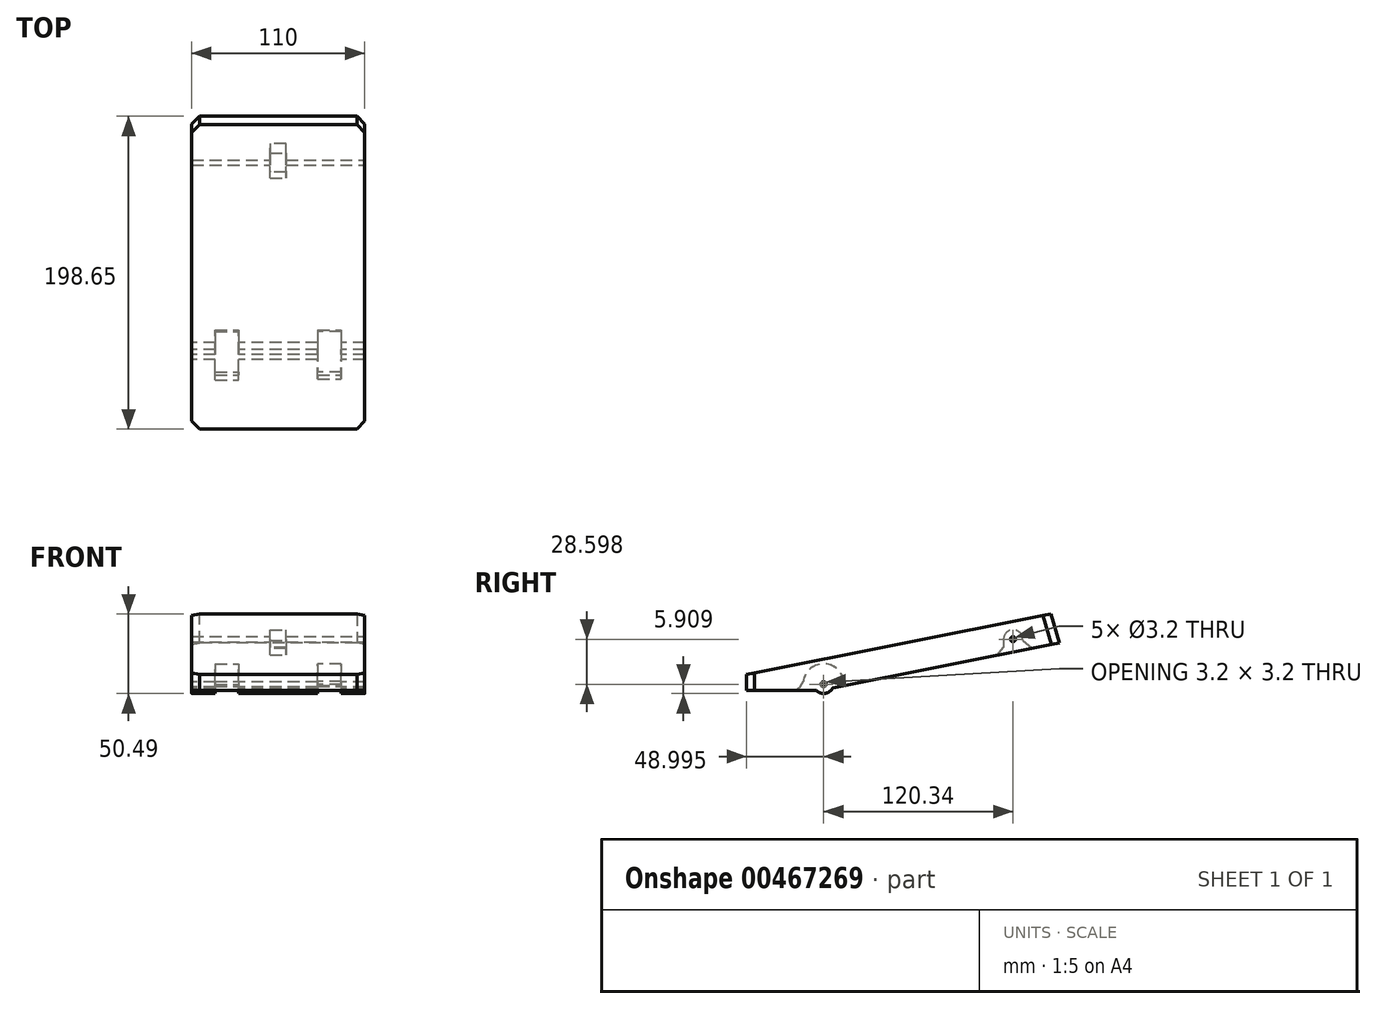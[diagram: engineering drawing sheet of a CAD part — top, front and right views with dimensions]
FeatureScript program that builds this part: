
annotation { "Feature Type Name" : "Feature", "Feature Type Description" : "" }
export const myFeature = defineFeature(function(context is Context, id is Id, definition is map)
    precondition{}
    {
        {
            var Q0;
            Q0=qCreatedBy(makeId("Right.planeOp"),FACE);
            cPlane(context, id + "F0", {"entities" : qUnion([Q0]), "cplaneType" : CPlaneType.OFFSET, "offset" : 55 * mm, "width" : 150 * mm, "height" : 150 * mm});
        }
        {
            var Q0;
            Q0=qCreatedBy(makeId("Right.planeOp"),FACE);
            var sketch = newSketch(context, id + "F1", { "sketchPlane" : qUnion([Q0])});
            skCircle(sketch, "E0.0", {"center": v(-48.56, 3.8) * mm, "radius": 1.6 * mm});
            skArc(sketch, "E1", {"start": v(-53.35, 0) * mm, "mid": v(-47.61, -2.03) * mm, "end": v(-42.71, 1.57) * mm});
            skLineSegment(sketch, "E2", {"start": v(-42.71, 1.57) * mm, "end": v(101.09, 30.13) * mm});
            skLineSegment(sketch, "E3", {"start": v(-97.56, 0) * mm, "end": v(-97.56, 10) * mm});
            skLineSegment(sketch, "E4", {"start": v(-97.56, 10) * mm, "end": v(95.78, 48.39) * mm});
            skLineSegment(sketch, "E5", {"start": v(-53.35, 0) * mm, "end": v(-97.56, 0) * mm});
            skLineSegment(sketch, "E6", {"start": v(95.78, 48.39) * mm, "end": v(101.09, 30.13) * mm});
            skSolve(sketch);
        }
        {
            var Q0;
            Q0=qSketchRegion(id+"F1",true);
            extrude(context, id + "F2", {"entities" : qUnion([Q0]), "depth" : 110 * mm});
        }
        {
            var Q0;
            Q0=qCreatedBy(makeId("Top.planeOp"),FACE);
            var sketch = newSketch(context, id + "F3", { "sketchPlane" : qUnion([Q0])});
            skLineSegment(sketch, "E7.bottom", {"start": v(15, -55.85) * mm, "end": v(30, -55.85) * mm});
            skLineSegment(sketch, "E7.top", {"start": v(15, -40.85) * mm, "end": v(30, -40.85) * mm});
            skLineSegment(sketch, "E7.left", {"start": v(15, -55.85) * mm, "end": v(15, -40.85) * mm});
            skLineSegment(sketch, "E7.right", {"start": v(30, -55.85) * mm, "end": v(30, -40.85) * mm});
            skLineSegment(sketch, "E8.bottom", {"start": v(80, -55.21) * mm, "end": v(95, -55.21) * mm});
            skLineSegment(sketch, "E8.top", {"start": v(80, -40.21) * mm, "end": v(95, -40.21) * mm});
            skLineSegment(sketch, "E8.left", {"start": v(80, -55.21) * mm, "end": v(80, -40.21) * mm});
            skLineSegment(sketch, "E8.right", {"start": v(95, -55.21) * mm, "end": v(95, -40.21) * mm});
            skSolve(sketch);
        }
        {
            var Q0;
            Q0=qSketchRegion(id+"F3",true);
            extrude(context, id + "F4", {"entities" : qUnion([Q0]), "operationType" : NewBodyOperationType.REMOVE, "endBound" : BoundingType.SYMMETRIC, "depth" : 21 * mm});
        }
        {
            var Q0;
            Q0=makeQuery(id+"F4.boolean.opBoolean","COPY",FACE,{"derivedFrom":makeQuery(id+"F4.opExtrude","SWEPT_FACE",FACE,{"disambiguationData":[OSD([sQuery(id+"F3.wireOp",EDGE,"E8.left")])]})});
            var sketch = newSketch(context, id + "F5", { "sketchPlane" : qUnion([Q0])});
            skCircle(sketch, "E9.0", {"center": v(-48.56, 3.8) * mm, "radius": 1.6 * mm});
            skArc(sketch, "E10", {"start": v(-35.56, 3.8) * mm, "mid": v(-48.56, 16.8) * mm, "end": v(-61.56, 3.8) * mm});
            skPoint(sketch, "E11.orphan", {"position": v(-97.56, 0) * mm});
            skPoint(sketch, "E12.orphan", {"position": v(-42.71, 1.57) * mm});
            skPoint(sketch, "E13.0.start.orphan", {"position": v(-53.35, 0) * mm});
            skLineSegment(sketch, "E14", {"start": v(-61.56, 3.8) * mm, "end": v(-67.66, -1.5) * mm});
            skLineSegment(sketch, "E15", {"start": v(-67.66, -1.5) * mm, "end": v(-44.57, -13.85) * mm});
            skLineSegment(sketch, "E16", {"start": v(-44.57, -13.85) * mm, "end": v(-28.97, -1.5) * mm});
            skLineSegment(sketch, "E17", {"start": v(-28.97, -1.5) * mm, "end": v(-35.56, 3.8) * mm});
            skPoint(sketch, "E18.end.orphan", {"position": v(0, 3.8) * mm});
            skPoint(sketch, "E19.end.orphan", {"position": v(-61.56, 0) * mm});
            skSolve(sketch);
        }
        {
            var Q0;
            Q0=qSketchRegion(id+"F5",true);
            var Q1;
            Q1=makeQuery(id+"F4.boolean.opBoolean","INTERSECT",VERTEX,{"derivedFrom":[makeQuery(id+"F2.opExtrude","SWEPT_FACE",FACE,{"disambiguationData":[OSD([sQuery(id+"F1.wireOp",EDGE,"E5")])]}),makeQuery(id+"F4.opExtrude","SWEPT_FACE",FACE,{"disambiguationData":[OSD([sQuery(id+"F3.wireOp",EDGE,"E8.bottom")])]}),makeQuery(id+"F4.opExtrude","SWEPT_FACE",FACE,{"disambiguationData":[OSD([sQuery(id+"F3.wireOp",EDGE,"E8.right")])]})]});
            extrude(context, id + "F6", {"entities" : qUnion([Q0]), "operationType" : NewBodyOperationType.REMOVE, "endBound" : BoundingType.UP_TO_VERTEX, "endBoundEntityVertex" : qUnion([Q1]), "depth" : 25 * mm});
        }
        {
            var Q0;
            Q0=makeQuery(id+"F6.boolean.opBoolean","COPY",EDGE,{"derivedFrom":makeQuery(id+"F6.opExtrude","SWEPT_EDGE",EDGE,{"disambiguationData":[OSD([sQuery(id+"F5.wireOp",EDGE,"E10"),sQuery(id+"F5.wireOp",EDGE,"E14")])]})});
            chamfer(context, id + "F7", {"entities" : qUnion([Q0]), "width" : 5 * mm, "tangentPropagation" : true});
        }
        {
            var Q0;
            Q0=qCreatedBy(id+"F0.planeOp",FACE);
            var sketch = newSketch(context, id + "F8", { "sketchPlane" : qUnion([Q0])});
            skArc(sketch, "E20", {"start": v(77.78, 32.4) * mm, "mid": v(71.78, 38.4) * mm, "end": v(65.78, 32.4) * mm});
            skLineSegment(sketch, "E21", {"start": v(65.78, 32.4) * mm, "end": v(65.78, 22.07) * mm});
            skLineSegment(sketch, "E22", {"start": v(77.78, 32.4) * mm, "end": v(77.78, 22.07) * mm});
            skLineSegment(sketch, "E23", {"start": v(65.78, 22.07) * mm, "end": v(77.78, 22.07) * mm});
            skSolve(sketch);
        }
        {
            var Q0;
            Q0=qSketchRegion(id+"F8",true);
            extrude(context, id + "F9", {"entities" : qUnion([Q0]), "operationType" : NewBodyOperationType.REMOVE, "endBound" : BoundingType.SYMMETRIC, "oppositeDirection" : true, "depth" : 10 * mm});
        }
        {
            var Q0;
            Q0=makeQuery(id+"F2.opExtrude","CAP_FACE",FACE,{"disambiguationData":[OSD([sQuery(id+"F1.wireOp",EDGE,"E0.0"),sQuery(id+"F1.wireOp",EDGE,"E1"),sQuery(id+"F1.wireOp",EDGE,"E2"),sQuery(id+"F1.wireOp",EDGE,"E3"),sQuery(id+"F1.wireOp",EDGE,"E4"),sQuery(id+"F1.wireOp",EDGE,"E5"),sQuery(id+"F1.wireOp",EDGE,"E6")])],"isStart":false});
            var sketch = newSketch(context, id + "F10", { "sketchPlane" : qUnion([Q0])});
            skCircle(sketch, "E24", {"center": v(71.78, 32.4) * mm, "radius": 1.6 * mm});
            skSolve(sketch);
        }
        {
            var Q0;
            Q0=qSketchRegion(id+"F10",true);
            extrude(context, id + "F11", {"entities" : qUnion([Q0]), "operationType" : NewBodyOperationType.REMOVE, "endBound" : BoundingType.THROUGH_ALL, "oppositeDirection" : true, "depth" : 25 * mm});
        }
        {
            var Q0;
            Q0=makeQuery(id+"F9.boolean.opBoolean","INTERSECT",EDGE,{"derivedFrom":[makeQuery(id+"F2.opExtrude","SWEPT_FACE",FACE,{"disambiguationData":[OSD([sQuery(id+"F1.wireOp",EDGE,"E2")])]}),makeQuery(id+"F9.opExtrude","SWEPT_FACE",FACE,{"disambiguationData":[OSD([sQuery(id+"F8.wireOp",EDGE,"E22")])]})]});
            chamfer(context, id + "F12", {"entities" : qUnion([Q0]), "width" : 5 * mm, "tangentPropagation" : true});
        }
        {
            var Q0;
            Q0=makeQuery(id+"F9.boolean.opBoolean","INTERSECT",EDGE,{"derivedFrom":[makeQuery(id+"F2.opExtrude","SWEPT_FACE",FACE,{"disambiguationData":[OSD([sQuery(id+"F1.wireOp",EDGE,"E2")])]}),makeQuery(id+"F9.opExtrude","SWEPT_FACE",FACE,{"disambiguationData":[OSD([sQuery(id+"F8.wireOp",EDGE,"E21")])]})]});
            chamfer(context, id + "F13", {"entities" : qUnion([Q0]), "width" : 5 * mm, "tangentPropagation" : true});
        }
        {
            var Q0;
            Q0=makeQuery(id+"F2.opExtrude","CAP_EDGE",EDGE,{"disambiguationData":[OSD([sQuery(id+"F1.wireOp",EDGE,"E6")])],"isStart":true});
            var Q1;
            Q1=makeQuery(id+"F2.opExtrude","CAP_EDGE",EDGE,{"disambiguationData":[OSD([sQuery(id+"F1.wireOp",EDGE,"E6")])],"isStart":false});
            var Q2;
            Q2=makeQuery(id+"FGveSszX63l5Zby_1.opExtrude","SWEPT_EDGE",EDGE,{"disambiguationData":[OSD([sQuery(id+"FY0ePOpRv7rLsL8_1.wireOp",EDGE,"3aef1af1-6b21-466a-8fd8-9d0ddb00b942.2"),sQuery(id+"FY0ePOpRv7rLsL8_1.wireOp",EDGE,"3aef1af1-6b21-466a-8fd8-9d0ddb00b942.3")])]});
            var Q3;
            Q3=makeQuery(id+"F2.opExtrude","CAP_EDGE",EDGE,{"disambiguationData":[OSD([sQuery(id+"F1.wireOp",EDGE,"E3")])],"isStart":false});
            var Q4;
            Q4=makeQuery(id+"F2.opExtrude","CAP_EDGE",EDGE,{"disambiguationData":[OSD([sQuery(id+"F1.wireOp",EDGE,"E3")])],"isStart":true});
            var Q5;
            Q5=makeQuery(id+"FGveSszX63l5Zby_1.opExtrude","SWEPT_EDGE",EDGE,{"disambiguationData":[OSD([sQuery(id+"FY0ePOpRv7rLsL8_1.wireOp",EDGE,"3aef1af1-6b21-466a-8fd8-9d0ddb00b942.0"),sQuery(id+"FY0ePOpRv7rLsL8_1.wireOp",EDGE,"3aef1af1-6b21-466a-8fd8-9d0ddb00b942.3")])]});
            var Q6;
            Q6=makeQuery(id+"FGveSszX63l5Zby_1.opExtrude","SWEPT_EDGE",EDGE,{"disambiguationData":[OSD([sQuery(id+"FY0ePOpRv7rLsL8_1.wireOp",EDGE,"dcda5d86-7792-4639-b30c-51c4dd1823a3.2"),sQuery(id+"FY0ePOpRv7rLsL8_1.wireOp",EDGE,"dcda5d86-7792-4639-b30c-51c4dd1823a3.3")])]});
            var Q7;
            Q7=makeQuery(id+"FGveSszX63l5Zby_1.opExtrude","SWEPT_EDGE",EDGE,{"disambiguationData":[OSD([sQuery(id+"FY0ePOpRv7rLsL8_1.wireOp",EDGE,"dcda5d86-7792-4639-b30c-51c4dd1823a3.0"),sQuery(id+"FY0ePOpRv7rLsL8_1.wireOp",EDGE,"dcda5d86-7792-4639-b30c-51c4dd1823a3.3")])]});
            var Q8;
            Q8=makeQuery(id+"FGveSszX63l5Zby_1.opExtrude","SWEPT_EDGE",EDGE,{"disambiguationData":[OSD([sQuery(id+"FY0ePOpRv7rLsL8_1.wireOp",EDGE,"dcda5d86-7792-4639-b30c-51c4dd1823a3.0"),sQuery(id+"FY0ePOpRv7rLsL8_1.wireOp",EDGE,"dcda5d86-7792-4639-b30c-51c4dd1823a3.1")])]});
            var Q9;
            Q9=makeQuery(id+"FGveSszX63l5Zby_1.opExtrude","SWEPT_EDGE",EDGE,{"disambiguationData":[OSD([sQuery(id+"FY0ePOpRv7rLsL8_1.wireOp",EDGE,"dcda5d86-7792-4639-b30c-51c4dd1823a3.1"),sQuery(id+"FY0ePOpRv7rLsL8_1.wireOp",EDGE,"dcda5d86-7792-4639-b30c-51c4dd1823a3.2")])]});
            chamfer(context, id + "F14", {"entities" : qUnion([Q0, Q1, Q2, Q3, Q4, Q5, Q6, Q7, Q8, Q9]), "width" : 5 * mm, "tangentPropagation" : true});
        }
        {
            var Q0;
            Q0=makeQuery(id+"F4.boolean.opBoolean","COPY",FACE,{"derivedFrom":makeQuery(id+"F4.opExtrude","SWEPT_FACE",FACE,{"disambiguationData":[OSD([sQuery(id+"F3.wireOp",EDGE,"E7.right")])]})});
            var sketch = newSketch(context, id + "F15", { "sketchPlane" : qUnion([Q0])});
            skCircle(sketch, "E25.0", {"center": v(48.56, 3.8) * mm, "radius": 1.6 * mm});
            skArc(sketch, "E26", {"start": v(61.56, 3.8) * mm, "mid": v(48.56, 16.8) * mm, "end": v(35.56, 3.8) * mm});
            skPoint(sketch, "E27.orphan", {"position": v(178.92, 19.57) * mm});
            skPoint(sketch, "E28.0.start.orphan", {"position": v(40.43, -7.24) * mm});
            skPoint(sketch, "E29.0.start.orphan", {"position": v(29.8, -8.82) * mm});
            skLineSegment(sketch, "E30", {"start": v(35.56, 3.8) * mm, "end": v(29.47, -1.5) * mm});
            skLineSegment(sketch, "E31", {"start": v(29.47, -1.5) * mm, "end": v(52.56, -13.85) * mm});
            skLineSegment(sketch, "E32", {"start": v(52.56, -13.85) * mm, "end": v(68.16, -1.5) * mm});
            skLineSegment(sketch, "E33", {"start": v(68.16, -1.5) * mm, "end": v(61.56, 3.8) * mm});
            skPoint(sketch, "E34.end.orphan", {"position": v(21.58, -8.82) * mm});
            skSolve(sketch);
        }
        {
            var Q0;
            Q0=qSketchRegion(id+"F15",true);
            var Q1;
            Q1=makeQuery(id+"F4.boolean.opBoolean","INTERSECT",VERTEX,{"derivedFrom":[makeQuery(id+"F2.opExtrude","SWEPT_FACE",FACE,{"disambiguationData":[OSD([sQuery(id+"F1.wireOp",EDGE,"E5")])]}),makeQuery(id+"F4.opExtrude","SWEPT_FACE",FACE,{"disambiguationData":[OSD([sQuery(id+"F3.wireOp",EDGE,"E7.bottom")])]}),makeQuery(id+"F4.opExtrude","SWEPT_FACE",FACE,{"disambiguationData":[OSD([sQuery(id+"F3.wireOp",EDGE,"E7.left")])]})]});
            extrude(context, id + "F16", {"entities" : qUnion([Q0]), "operationType" : NewBodyOperationType.REMOVE, "endBound" : BoundingType.UP_TO_VERTEX, "endBoundEntityVertex" : qUnion([Q1]), "depth" : 25 * mm});
        }
        {
            var Q0;
            Q0=makeQuery(id+"F16.boolean.opBoolean","COPY",EDGE,{"derivedFrom":makeQuery(id+"F16.opExtrude","SWEPT_EDGE",EDGE,{"disambiguationData":[OSD([sQuery(id+"F15.wireOp",EDGE,"E26"),sQuery(id+"F15.wireOp",EDGE,"E33")])]})});
            chamfer(context, id + "F17", {"entities" : qUnion([Q0]), "width" : 5 * mm, "tangentPropagation" : true});
        }
    });
